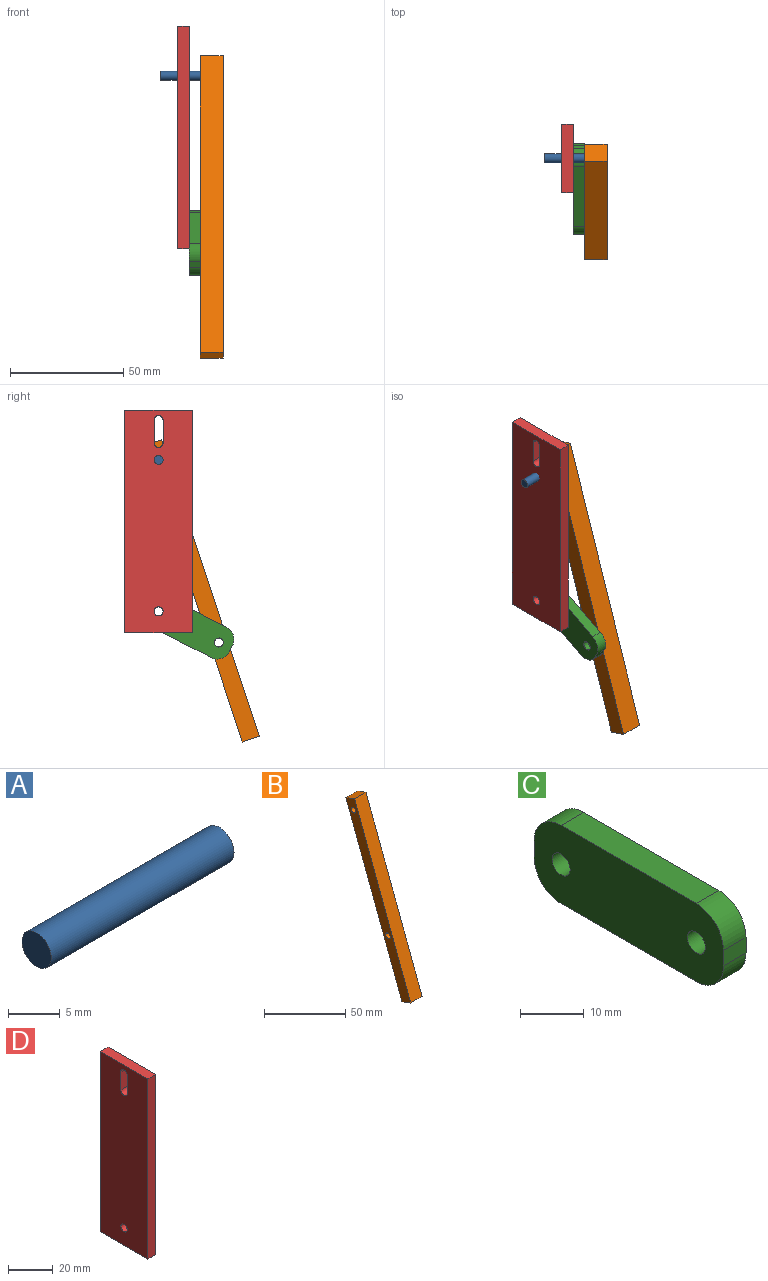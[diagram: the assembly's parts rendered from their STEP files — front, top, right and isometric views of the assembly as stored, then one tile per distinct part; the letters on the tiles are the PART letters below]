
ASSEMBLY  parts=4 mates=4
PART A: 3 faces, bbox 25x4x4 mm
  f0: plane 4x4mm, normal (1,0,0), area 12.6mm2, adj f2
  f1: plane 4x4mm, normal (-1,0,0), area 12.6mm2, adj f2
  f2: cylinder r=2mm len=25mm, axis (1,0,0), area 314.2mm2, adj f0,f1
PART B: 8 faces, bbox 10x56.2x131.9 mm
  f0: plane 10x7.49mm, normal (0,0.35,0.94), area 80mm2, adj f1,f3,f6,f7
  f1: plane 129.12x48.71mm, normal (0,-0.94,0.35), area 1380mm2, adj f0,f2,f6,f7
  f2: plane 10x7.49mm, normal (0,-0.35,-0.94), area 80mm2, adj f1,f3,f6,f7
  f3: plane 129.12x48.71mm, normal (0,0.94,-0.35), area 1380mm2, adj f0,f2,f6,f7
  f4: cylinder r=2mm len=10mm, axis (-1,0,0), area 125.7mm2, adj f6,f7
  f5: cylinder r=2mm len=10mm, axis (-1,0,0), area 125.7mm2, adj f6,f7
  f6: plane 131.94x56.19mm, normal (1,0,0), area 1078.9mm2, adj f0,f1,f2,f3,f4,f5
  f7: plane 131.94x56.19mm, normal (-1,0,0), area 1078.9mm2, adj f0,f1,f2,f3,f4,f5
PART C: 12 faces, bbox 5x42x15 mm
  f0: plane 5x3mm, normal (0,-1,0), area 15mm2, adj f1,f9,f10,f11
  f1: cylinder r=6mm len=6mm, axis (-1,0,0), area 47.1mm2, adj f0,f2,f10,f11
  f2: plane 30x5mm, normal (0,0,-1), area 150mm2, adj f1,f3,f10,f11
  f3: cylinder r=6mm len=6mm, axis (-1,0,0), area 47.1mm2, adj f2,f4,f10,f11
  f4: plane 5x3mm, normal (0,1,0), area 15mm2, adj f3,f5,f10,f11
  f5: cylinder r=6mm len=6mm, axis (-1,0,0), area 47.1mm2, adj f4,f6,f10,f11
  f6: plane 30x5mm, normal (0,0,1), area 150mm2, adj f5,f9,f10,f11
  f7: cylinder r=2mm len=5mm, axis (-1,0,0), area 62.8mm2, adj f10,f11
  f8: cylinder r=2mm len=5mm, axis (-1,0,0), area 62.8mm2, adj f10,f11
  f9: cylinder r=6mm len=6mm, axis (-1,0,0), area 47.1mm2, adj f0,f6,f10,f11
  f10: plane 42x15mm, normal (1,0,0), area 574mm2, adj f0,f1,f2,f3,f4,f5,f6,f7
  f11: plane 42x15mm, normal (-1,0,0), area 574mm2, adj f0,f1,f2,f3,f4,f5,f6,f7
PART D: 11 faces, bbox 5x30x98.5 mm
  f0: plane 30x5mm, normal (0,0,1), area 150mm2, adj f1,f8,f9,f10
  f1: plane 98.53x5mm, normal (0,-1,0), area 492.6mm2, adj f0,f2,f9,f10
  f2: plane 30x5mm, normal (0,0,-1), area 150mm2, adj f1,f8,f9,f10
  f3: cylinder r=2mm len=5mm, axis (1,0,0), area 31.4mm2, adj f4,f7,f9,f10
  f4: plane 10x5mm, normal (0,1,0), area 50mm2, adj f3,f5,f9,f10
  f5: cylinder r=2mm len=5mm, axis (1,0,0), area 31.4mm2, adj f4,f7,f9,f10
  f6: cylinder r=2mm len=5mm, axis (1,0,0), area 62.8mm2, adj f9,f10
  f7: plane 10x5mm, normal (0,-1,0), area 50mm2, adj f3,f5,f9,f10
  f8: plane 98.53x5mm, normal (0,1,0), area 492.6mm2, adj f0,f2,f9,f10
  f9: plane 98.53x30mm, normal (-1,0,0), area 2890.8mm2, adj f0,f1,f2,f3,f4,f5,f6,f7
  f10: plane 98.53x30mm, normal (1,0,0), area 2890.8mm2, adj f0,f1,f2,f3,f4,f5,f6,f7
PLACE A rot(axis=(1,0,0),76.3deg) t=(-0.72,72.27,46.38)mm
PLACE B rot(axis=(1,0,0),2.4deg) t=(1.78,-1.67,-14.21)mm
PLACE C rot(axis=(1,0,0),27.3deg) t=(1.78,-4.99,-1.7)mm
PLACE D t=(1.78,-4.99,-1.7)mm fixed
MATE pin_slot A.f2 <-> D.f5  axis (1,0,0) through (1.78,-4.99,65.25)mm
MATE revolute D.f6 <-> C.f7  axis (1,0,0) through (1.78,-4.99,-1.7)mm
MATE revolute B.f5 <-> C.f8  axis (-1,0,0) through (6.78,-31.65,-15.46)mm
MATE cylindrical B.f4 <-> A.f2  axis (-1,0,0) through (16.78,-4.99,65.25)mm
